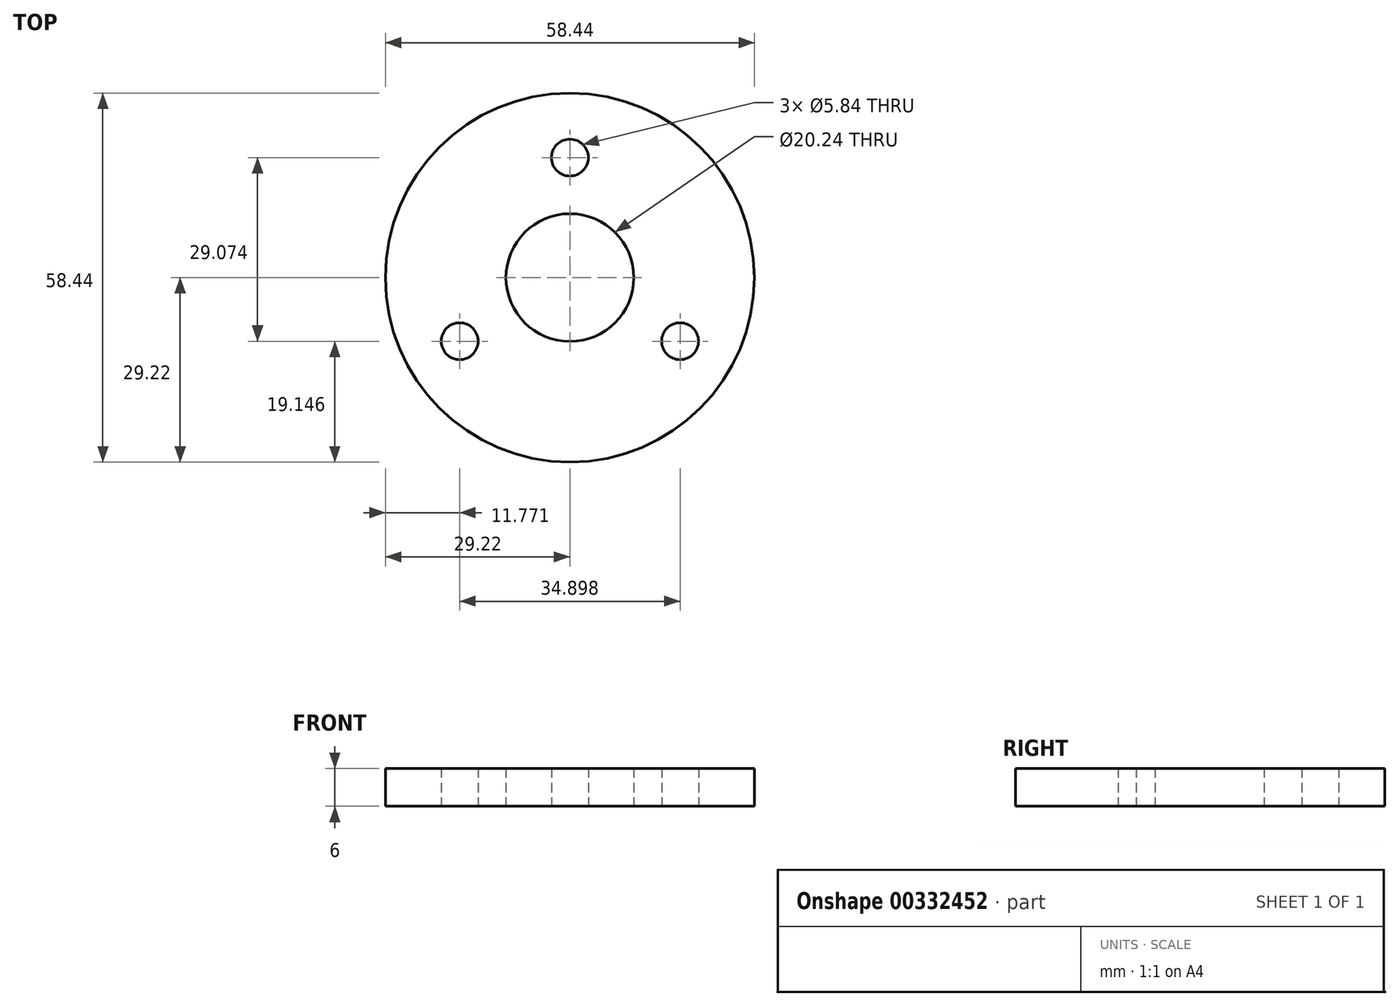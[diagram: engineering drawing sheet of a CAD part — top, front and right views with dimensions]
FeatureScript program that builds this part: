
annotation { "Feature Type Name" : "Feature", "Feature Type Description" : "" }
export const myFeature = defineFeature(function(context is Context, id is Id, definition is map)
    precondition{}
    {
        {
            var Q0;
            Q0=qCreatedBy(makeId("Top.planeOp"),FACE);
            var sketch = newSketch(context, id + "F0", { "sketchPlane" : qUnion([Q0])});
            skCircle(sketch, "E0", {"center": v(0, 0) * mm, "radius": 10.12 * mm});
            skCircle(sketch, "E1", {"center": v(0, 0) * mm, "radius": 29.22 * mm});
            skCircle(sketch, "E2", {"center": v(0, 19) * mm, "radius": 2.92 * mm});
            skCircle(sketch, "E3", {"center": v(-17.45, -10.07) * mm, "radius": 2.92 * mm});
            skCircle(sketch, "E4", {"center": v(17.45, -10.07) * mm, "radius": 2.92 * mm});
            skSolve(sketch);
        }
        {
            var Q0;
            Q0=makeQuery(id+"F0.imprint","IMPRINT",FACE,{"disambiguationData":[TD([[makeQuery(id+"F0.imprint","IMPRINT",EDGE,{"derivedFrom":sQuery(id+"F0.wireOp",EDGE,"E0")}),-1.0]])]});
            extrude(context, id + "F1", {"entities" : qUnion([Q0]), "depth" : 6 * mm});
        }
    });
